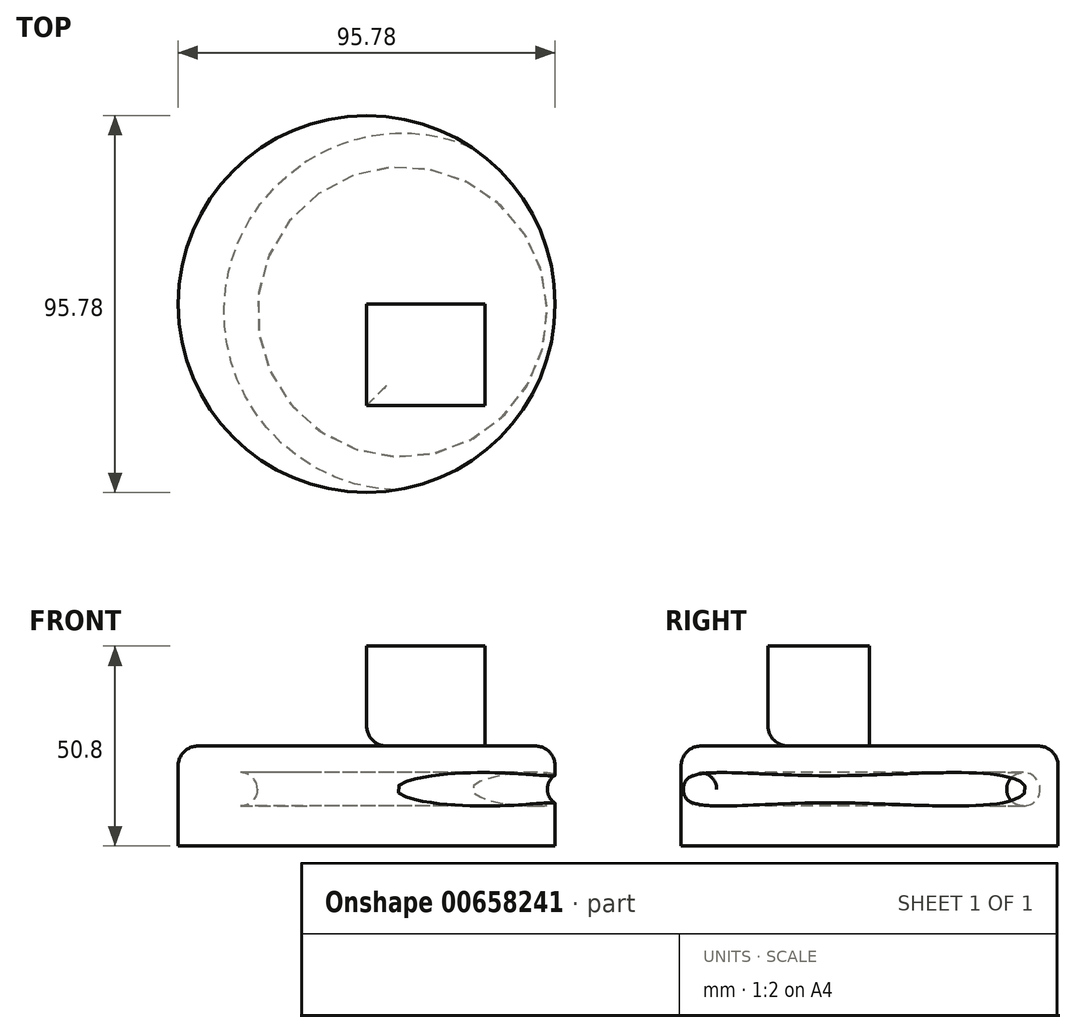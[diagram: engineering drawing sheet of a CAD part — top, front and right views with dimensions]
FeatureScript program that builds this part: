
annotation { "Feature Type Name" : "Feature", "Feature Type Description" : "" }
export const myFeature = defineFeature(function(context is Context, id is Id, definition is map)
    precondition{}
    {
        {
            var Q0;
            Q0=qCreatedBy(makeId("Top.planeOp"),FACE);
            cPlane(context, id + "F0", {"entities" : qUnion([Q0]), "cplaneType" : CPlaneType.OFFSET, "offset" : 50.8 * mm, "width" : 152.4 * mm, "height" : 152.4 * mm});
        }
        {
            var Q0;
            Q0=qCreatedBy(makeId("Top.planeOp"),FACE);
            var sketch = newSketch(context, id + "F1", { "sketchPlane" : qUnion([Q0])});
            skCircle(sketch, "E0", {"center": v(0, 0) * mm, "radius": 47.9 * mm});
            skSolve(sketch);
        }
        {
            var Q0;
            Q0=qCreatedBy(id+"F0.planeOp",FACE);
            var sketch = newSketch(context, id + "F2", { "sketchPlane" : qUnion([Q0])});
            skLineSegment(sketch, "E1.bottom", {"start": v(0, 0) * mm, "end": v(30.02, 0) * mm});
            skLineSegment(sketch, "E1.top", {"start": v(0, -25.8) * mm, "end": v(30.02, -25.8) * mm});
            skLineSegment(sketch, "E1.left", {"start": v(0, 0) * mm, "end": v(0, -25.8) * mm});
            skLineSegment(sketch, "E1.right", {"start": v(30.02, 0) * mm, "end": v(30.02, -25.8) * mm});
            skSolve(sketch);
        }
        {
            var Q0;
            Q0=makeQuery(id+"F1.imprint","IMPRINT",FACE,{"disambiguationData":[TD([[makeQuery(id+"F1.imprint","IMPRINT",EDGE,{"derivedFrom":sQuery(id+"F1.wireOp",EDGE,"E0")}),1.0]])]});
            extrude(context, id + "F3", {"entities" : qUnion([Q0]), "depth" : 25.4 * mm, "offsetDistance" : 25.4 * mm});
        }
        {
            var Q0;
            Q0=makeQuery(id+"F2.imprint","IMPRINT",FACE,{"disambiguationData":[TD([[makeQuery(id+"F2.imprint","IMPRINT",EDGE,{"derivedFrom":sQuery(id+"F2.wireOp",EDGE,"E1.bottom")}),-1.0]])]});
            extrude(context, id + "F4", {"entities" : qUnion([Q0]), "oppositeDirection" : true, "depth" : 25.4 * mm, "offsetDistance" : 25.4 * mm});
        }
        {
            var Q0;
            Q0=qCreatedBy(makeId("Top.planeOp"),FACE);
            cPlane(context, id + "F5", {"entities" : qUnion([Q0]), "cplaneType" : CPlaneType.OFFSET, "offset" : 12.7 * mm, "width" : 152.4 * mm, "height" : 152.4 * mm});
        }
        {
            var Q0;
            Q0=qCreatedBy(id+"F5.planeOp",FACE);
            var sketch = newSketch(context, id + "F6", { "sketchPlane" : qUnion([Q0])});
            skCircle(sketch, "E2", {"center": v(9.08, -2) * mm, "radius": 44.3 * mm});
            skSolve(sketch);
        }
        {
            var Q0;
            Q0=qCreatedBy(makeId("Front.planeOp"),FACE);
            var sketch = newSketch(context, id + "F7", { "sketchPlane" : qUnion([Q0])});
            skCircle(sketch, "E3", {"center": v(50.1, 14.4) * mm, "radius": 4.24 * mm});
            skSolve(sketch);
        }
        {
            var Q0;
            Q0=makeQuery(id+"F7.imprint","IMPRINT",FACE,{"disambiguationData":[TD([[makeQuery(id+"F7.imprint","IMPRINT",EDGE,{"derivedFrom":sQuery(id+"F7.wireOp",EDGE,"E3")}),1.0]])]});
            var Q1;
            Q1=sQuery(id+"F6.wireOp",EDGE,"E2");
            sweep(context, id + "F8", {"operationType" : NewBodyOperationType.REMOVE, "profiles" : qUnion([Q0]), "path" : qUnion([Q1])});
        }
        {
            var Q0;
            Q0=makeQuery(id+"F4.opExtrude","CAP_EDGE",EDGE,{"disambiguationData":[OSD([sQuery(id+"F2.wireOp",EDGE,"E1.left")])],"isStart":false});
            var Q1;
            Q1=makeQuery(id+"F3.opExtrude","CAP_EDGE",EDGE,{"disambiguationData":[OSD([sQuery(id+"F1.wireOp",EDGE,"E0")])],"isStart":false});
            var Q2;
            Q2=makeQuery(id+"F4.opExtrude","CAP_EDGE",EDGE,{"disambiguationData":[OSD([sQuery(id+"F2.wireOp",EDGE,"E1.top")])],"isStart":false});
            fillet(context, id + "F9", {"entities" : qUnion([Q0, Q1, Q2]), "radius" : 5.08 * mm, "tangentPropagation" : true, "allowEdgeOverflow" : false});
        }
    });
